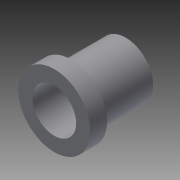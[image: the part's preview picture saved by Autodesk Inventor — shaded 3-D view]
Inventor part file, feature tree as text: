
AUTODESK INVENTOR PART (.ipt)
format: ipt  version: 2014 (Build 180170000, 170)  size: 105,984 bytes
history: native  units: in
note: dims shown in document units (in); Inventor stores cm internally (conversion verified against a paired STEP export)
features: sketch x3, extrude x3, plane x2, reference x1
ambient origin geometry x8: Origin, YZ Plane, XZ Plane, XY Plane, X Axis, Y Axis, Z Axis, Center Point
bodies: Solid1 (feature_tree)
feature tree (9):
  plane  "Work Plane1"
  sketch  "Sketch1"  dims[d0=0.01in d1=0.52in]
  plane  "Work Plane2"
  extrude  "Extrusion1"  Depth=0.52in
  extrude  "Extrusion2"  Depth=0.1in
  extrude  "Extrusion4"  Depth=0.1in
  reference  "Reference1"
  sketch  "Sketch2"  dims[d2=1.0in d3=0.0in d4=0.1in]
  sketch  "Sketch4"  dims[d5=0.2in d6=0.0in d9=0.1in d10=0.1in d11=0.0in]
